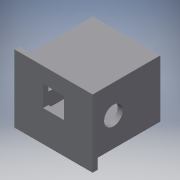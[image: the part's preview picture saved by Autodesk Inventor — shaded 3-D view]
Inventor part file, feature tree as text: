
AUTODESK INVENTOR PART (.ipt)
format: ipt  version: 2016 (Build 200138000, 138)  size: 136,192 bytes
history: native  units: mm
features: extrude x5, sketch x5
ambient origin geometry x8: Origin, YZ Plane, XZ Plane, XY Plane, X Axis, Y Axis, Z Axis, Center Point
bodies: Solid1 (feature_tree)
feature tree (10):
  extrude  "Extrusion1"  Depth=11.0mm
  extrude  "Extrusion2"  Depth=13.0mm
  extrude  "Extrusion3"  Depth=5.5mm
  extrude  "Extrusion4"  Depth=13.0mm TaperAngle=0.0deg
  extrude  "Extrusion5"  Depth=1.0mm
  sketch  "Sketch1"  dims[d0=13.0mm d1=11.0mm]
  sketch  "Sketch2"  dims[d2=13.0mm d3=0.0mm d4=3.6mm]
  sketch  "Sketch3"  dims[d5=4.0mm d7=5.5mm]
  sketch  "Sketch4"  dims[d8=5.5mm d9=13.0mm d10=0.0mm]
  sketch  "Sketch5"  dims[d11=1.0mm d12=1.0mm d14=1.0mm d15=1.0mm d16=13.0mm d17=0.0mm d18=1.0mm d19=1.0mm d20=1.0mm d21=1.0mm d22=1.0mm d23=0.0mm d27=2.0mm d28=4.0mm d29=4.0mm d30=3.0mm d31=7.5mm d32=1.0mm d33=0.0mm]
